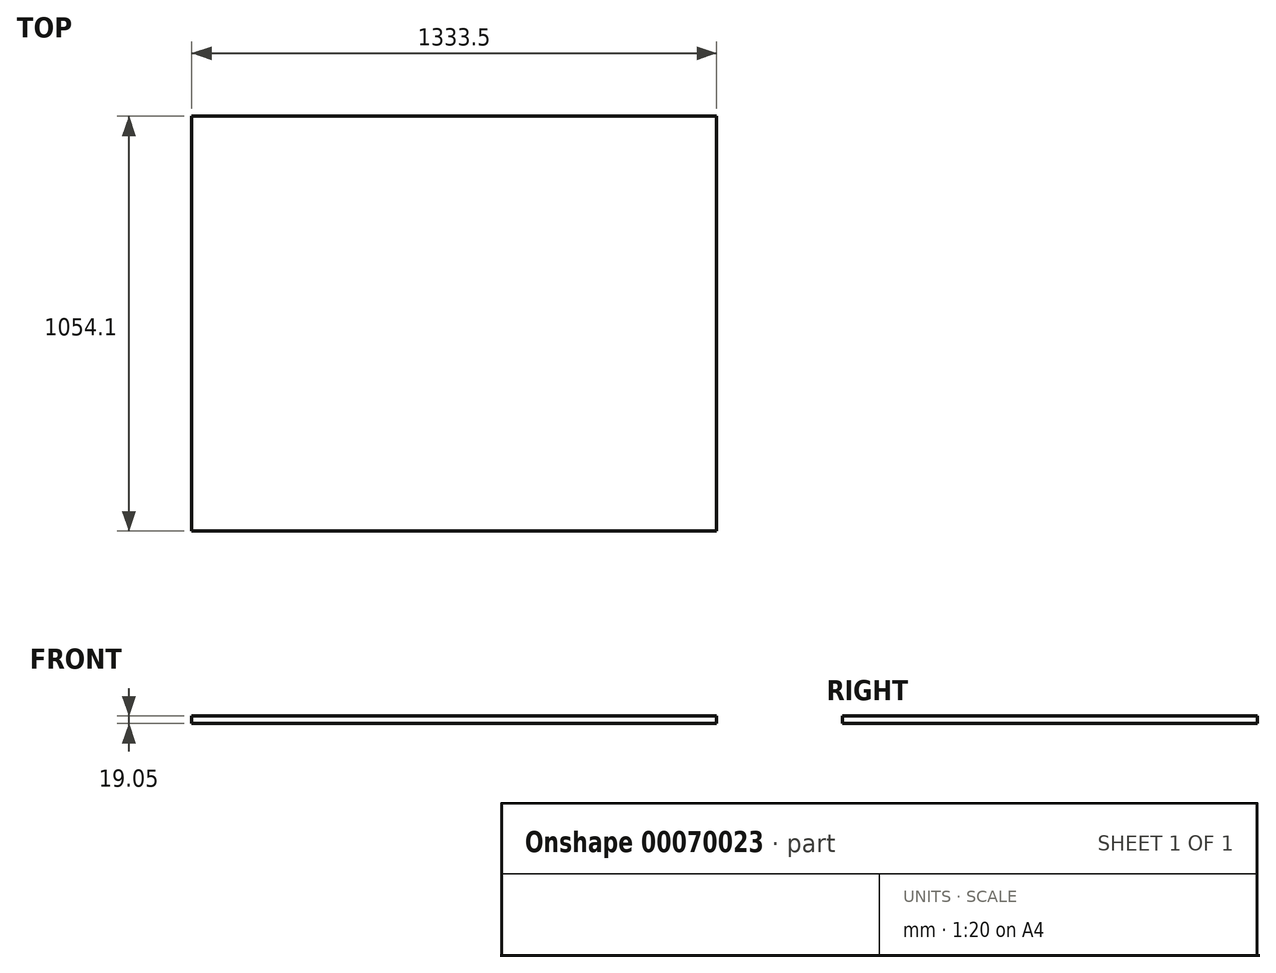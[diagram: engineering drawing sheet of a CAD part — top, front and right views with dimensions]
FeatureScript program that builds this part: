
annotation { "Feature Type Name" : "Feature", "Feature Type Description" : "" }
export const myFeature = defineFeature(function(context is Context, id is Id, definition is map)
    precondition{}
    {
        {
            var Q0;
            Q0=qCreatedBy(makeId("Top.planeOp"),FACE);
            var sketch = newSketch(context, id + "F0", { "sketchPlane" : qUnion([Q0])});
            skLineSegment(sketch, "E0.bottom", {"start": v(0, 0) * mm, "end": v(1333.5, 0) * mm});
            skLineSegment(sketch, "E0.top", {"start": v(0, 1054.1) * mm, "end": v(1333.5, 1054.1) * mm});
            skLineSegment(sketch, "E0.left", {"start": v(0, 0) * mm, "end": v(0, 1054.1) * mm});
            skLineSegment(sketch, "E0.right", {"start": v(1333.5, 0) * mm, "end": v(1333.5, 1054.1) * mm});
            skSolve(sketch);
        }
        {
            var Q0;
            Q0=makeQuery(id+"F0.imprint","IMPRINT",FACE,{"disambiguationData":[TD([[makeQuery(id+"F0.imprint","IMPRINT",EDGE,{"derivedFrom":sQuery(id+"F0.wireOp",EDGE,"E0.bottom")}),1.0]])]});
            extrude(context, id + "F1", {"entities" : qUnion([Q0]), "depth" : 19.05 * mm});
        }
    });
